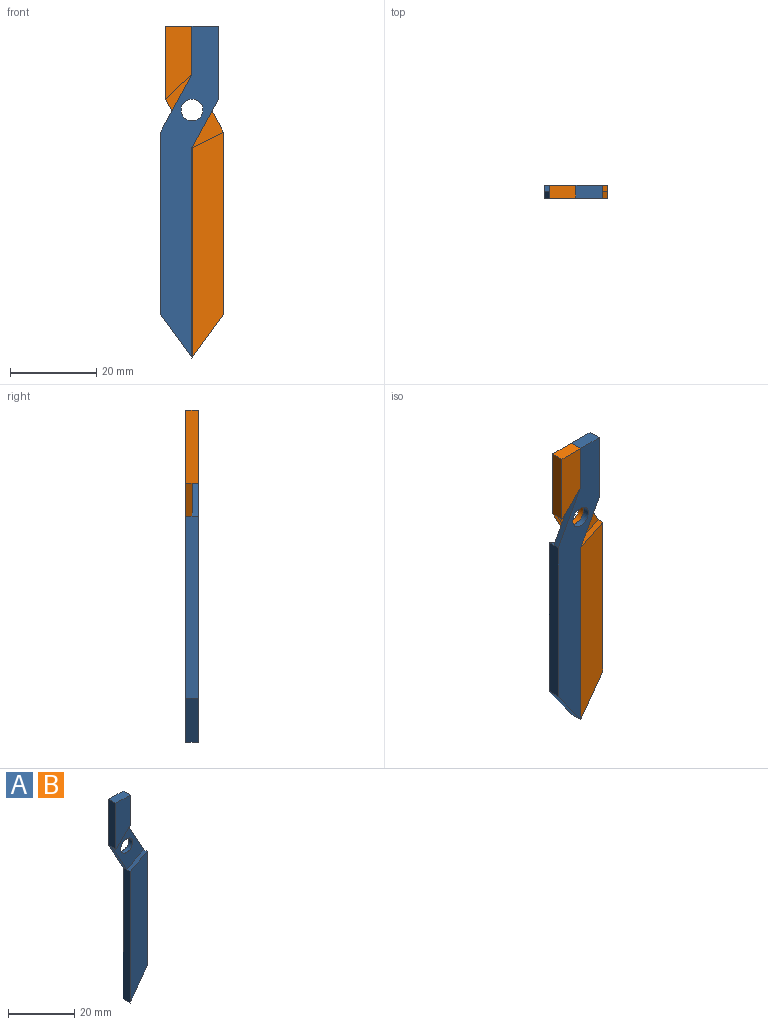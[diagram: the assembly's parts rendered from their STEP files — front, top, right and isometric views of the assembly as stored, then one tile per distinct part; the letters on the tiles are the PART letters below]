
ASSEMBLY  parts=2 mates=1
PART A: 15 faces, bbox 13.4x3x76.8 mm
  f0: plane 11.2x6.1mm, normal (-0.88,0,-0.48), area 19.1mm2, adj f4,f9,f11,f14
  f1: plane 13.38x7.28mm, normal (0.88,0,0.48), area 22.8mm2, adj f6,f7,f11,f14
  f2: cylinder r=2.52mm len=5.05mm, axis (0,1,0), area 23.8mm2, adj f11,f14
  f3: plane 17.01x6.1mm, normal (0,-1,0), area 85.9mm2, adj f7,f8,f9,f12
  f4: plane 48.63x3mm, normal (-1,0,0), area 145.9mm2, adj f0,f5,f10,f11,f13
  f5: plane 10.12x7.28mm, normal (0.81,0,-0.58), area 37.4mm2, adj f4,f6,f10,f11
  f6: plane 42.17x3mm, normal (1,0,0), area 126.5mm2, adj f1,f5,f10,f11,f13
  f7: plane 11.17x3mm, normal (1,0,0), area 33.5mm2, adj f1,f3,f8,f11,f12
  f8: plane 6.1x3mm, normal (0,0,1), area 18.3mm2, adj f3,f7,f9,f11
  f9: plane 17.01x3mm, normal (-1,0,0), area 51mm2, adj f0,f3,f8,f11,f12
  f10: plane 52.29x7.28mm, normal (0,-1,0), area 330.6mm2, adj f4,f5,f6,f13
  f11: plane 76.84x13.38mm, normal (0,1,0), area 510.5mm2, adj f0,f1,f2,f4,f5,f6,f7,f8
  f12: plane 6.1x5.84mm, normal (0.69,0,-0.72), area 12.7mm2, adj f3,f7,f9,f14
  f13: plane 7.28x3.67mm, normal (-0.45,0,0.89), area 12.2mm2, adj f4,f6,f10,f14
  f14: plane 17.04x13.38mm, normal (0,-1,0), area 94mm2, adj f0,f1,f2,f12,f13
PART B: same geometry as A
PLACE A rot(axis=(0,0,1),180deg) t=(-15.62,-2.87,33.6)mm
PLACE B t=(-15.62,0.13,33.6)mm fixed
MATE revolute A.f2 <-> B.f2  axis (0,1,0) through (-15.62,-1.37,25.33)mm
